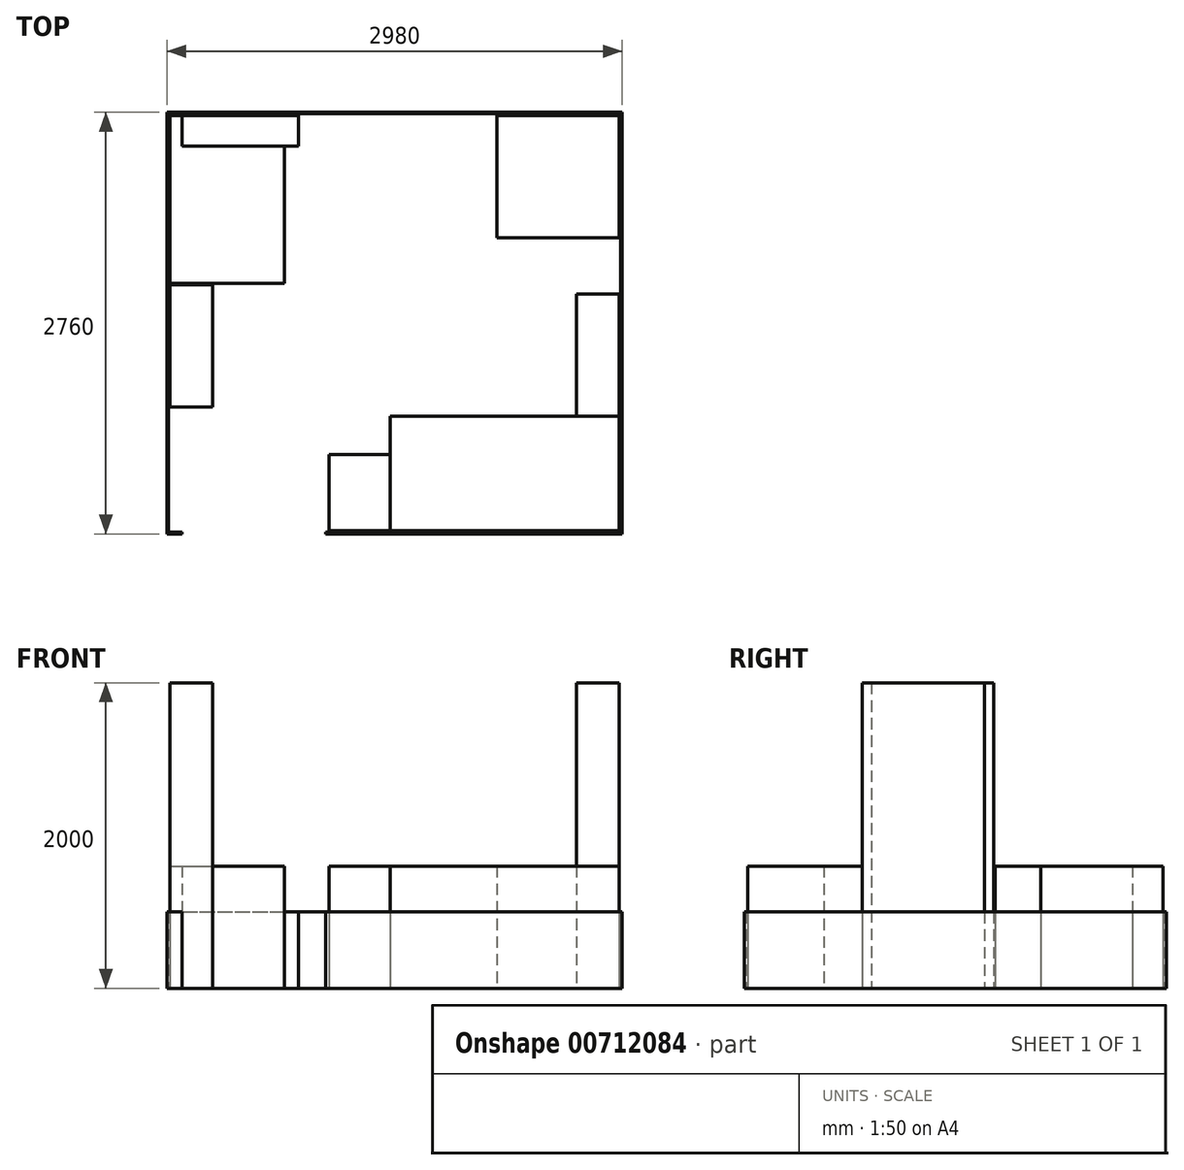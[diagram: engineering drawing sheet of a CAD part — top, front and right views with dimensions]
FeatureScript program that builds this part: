
annotation { "Feature Type Name" : "Feature", "Feature Type Description" : "" }
export const myFeature = defineFeature(function(context is Context, id is Id, definition is map)
    precondition{}
    {
        {
            var Q0;
            Q0=qCreatedBy(makeId("Top.planeOp"),FACE);
            var sketch = newSketch(context, id + "F0", { "sketchPlane" : qUnion([Q0])});
            skLineSegment(sketch, "E0.bottom", {"start": v(-1490, 1990) * mm, "end": v(1470, 1990) * mm});
            skLineSegment(sketch, "E0.top", {"start": v(-1490, -750) * mm, "end": v(-1400, -750) * mm});
            skLineSegment(sketch, "E0.left", {"start": v(-1490, 1990) * mm, "end": v(-1490, -750) * mm});
            skLineSegment(sketch, "E0.right", {"start": v(1470, 1990) * mm, "end": v(1470, -750) * mm});
            skLineSegment(sketch, "E1.0", {"start": v(-1500, 2000) * mm, "end": v(-1500, -760) * mm});
            skLineSegment(sketch, "E1.1", {"start": v(-1500, 2000) * mm, "end": v(1480, 2000) * mm});
            skLineSegment(sketch, "E1.2", {"start": v(1480, 2000) * mm, "end": v(1480, -760) * mm});
            skLineSegment(sketch, "E1.3", {"start": v(-1500, -760) * mm, "end": v(-1400, -760) * mm});
            skLineSegment(sketch, "E2", {"start": v(-1400, -750) * mm, "end": v(-1400, -760) * mm});
            skLineSegment(sketch, "E3", {"start": v(-460, -750) * mm, "end": v(-460, -760) * mm});
            skLineSegment(sketch, "E4.trimOffspring", {"start": v(-460, -750) * mm, "end": v(1470, -750) * mm});
            skLineSegment(sketch, "E5.trimOffspring", {"start": v(-460, -760) * mm, "end": v(1480, -760) * mm});
            skLineSegment(sketch, "E6.bottom", {"start": v(1180, 810) * mm, "end": v(1460, 810) * mm});
            skLineSegment(sketch, "E6.top", {"start": v(1180, 10) * mm, "end": v(1460, 10) * mm});
            skLineSegment(sketch, "E6.left", {"start": v(1180, 810) * mm, "end": v(1180, 10) * mm});
            skLineSegment(sketch, "E6.right", {"start": v(1460, 810) * mm, "end": v(1460, 10) * mm});
            skLineSegment(sketch, "E7.bottom", {"start": v(-1480, 70) * mm, "end": v(-1200, 70) * mm});
            skLineSegment(sketch, "E7.top", {"start": v(-1480, 870) * mm, "end": v(-1200, 870) * mm});
            skLineSegment(sketch, "E7.left", {"start": v(-1480, 70) * mm, "end": v(-1480, 870) * mm});
            skLineSegment(sketch, "E7.right", {"start": v(-1200, 70) * mm, "end": v(-1200, 870) * mm});
            skLineSegment(sketch, "E8.bottom", {"start": v(660, 1980) * mm, "end": v(1460, 1980) * mm});
            skLineSegment(sketch, "E8.top", {"start": v(660, 1180) * mm, "end": v(1460, 1180) * mm});
            skLineSegment(sketch, "E8.left", {"start": v(660, 1980) * mm, "end": v(660, 1180) * mm});
            skLineSegment(sketch, "E8.right", {"start": v(1460, 1980) * mm, "end": v(1460, 1180) * mm});
            skLineSegment(sketch, "E9.bottom", {"start": v(-40, -740) * mm, "end": v(1460, -740) * mm});
            skLineSegment(sketch, "E9.top", {"start": v(-40, 10) * mm, "end": v(1460, 10) * mm});
            skLineSegment(sketch, "E9.left", {"start": v(-40, -740) * mm, "end": v(-40, 10) * mm});
            skLineSegment(sketch, "E9.right", {"start": v(1460, -740) * mm, "end": v(1460, 10) * mm});
            skLineSegment(sketch, "E10.bottom", {"start": v(-1400, 1980) * mm, "end": v(-640, 1980) * mm});
            skLineSegment(sketch, "E10.top", {"start": v(-1400, 1780) * mm, "end": v(-640, 1780) * mm});
            skLineSegment(sketch, "E10.left", {"start": v(-1400, 1980) * mm, "end": v(-1400, 1780) * mm});
            skLineSegment(sketch, "E10.right", {"start": v(-640, 1980) * mm, "end": v(-640, 1780) * mm});
            skLineSegment(sketch, "E11.bottom", {"start": v(-1480, 1980) * mm, "end": v(-730, 1980) * mm});
            skLineSegment(sketch, "E11.top", {"start": v(-1480, 880) * mm, "end": v(-730, 880) * mm});
            skLineSegment(sketch, "E11.left", {"start": v(-1480, 1980) * mm, "end": v(-1480, 880) * mm});
            skLineSegment(sketch, "E11.right", {"start": v(-730, 1980) * mm, "end": v(-730, 880) * mm});
            skLineSegment(sketch, "E12.bottom", {"start": v(-440, -740) * mm, "end": v(-40, -740) * mm});
            skLineSegment(sketch, "E12.top", {"start": v(-440, -240) * mm, "end": v(-40, -240) * mm});
            skLineSegment(sketch, "E12.left", {"start": v(-440, -740) * mm, "end": v(-440, -240) * mm});
            skLineSegment(sketch, "E12.right", {"start": v(-40, -740) * mm, "end": v(-40, -240) * mm});
            skSolve(sketch);
        }
        {
            var Q0;
            Q0=makeQuery(id+"F0.imprint","IMPRINT",FACE,{"disambiguationData":[TD([[makeQuery(id+"F0.imprint","IMPRINT",EDGE,{"derivedFrom":sQuery(id+"F0.wireOp",EDGE,"E0.bottom")}),1.0]])]});
            extrude(context, id + "F1", {"entities" : qUnion([Q0]), "depth" : 500 * mm, "offsetDistance" : 25 * mm});
        }
        {
            var Q0;
            Q0=makeQuery(id+"F0.imprint","IMPRINT",FACE,{"disambiguationData":[TD([[makeQuery(id+"F0.imprint","IMPRINT",EDGE,{"derivedFrom":sQuery(id+"F0.wireOp",EDGE,"E7.bottom")}),1.0]])]});
            extrude(context, id + "F2", {"entities" : qUnion([Q0]), "depth" : 2000 * mm, "offsetDistance" : 25 * mm});
        }
        {
            var Q0;
            Q0=makeQuery(id+"F0.imprint","IMPRINT",FACE,{"disambiguationData":[TD([[makeQuery(id+"F0.imprint","IMPRINT",EDGE,{"derivedFrom":sQuery(id+"F0.wireOp",EDGE,"E10.bottom")}),-1.0]])]});
            extrude(context, id + "F3", {"entities" : qUnion([Q0]), "depth" : 500 * mm, "offsetDistance" : 25 * mm});
        }
        {
            var Q0;
            Q0=makeQuery(id+"F0.imprint","IMPRINT",FACE,{"disambiguationData":[TD([[makeQuery(id+"F0.imprint","IMPRINT",EDGE,{"derivedFrom":sQuery(id+"F0.wireOp",EDGE,"E11.bottom")}),-1.0]])]});
            var Q1;
            {var subQ2=sQuery(id+"F0.wireOp",EDGE,"E10.left");Q1=makeQuery(id+"F0.imprint","IMPRINT",FACE,{"disambiguationData":[TD([[makeQuery(id+"F0.imprint","IMPRINT",EDGE,{"derivedFrom":subQ2}),-1.0]])]});}
            extrude(context, id + "F4", {"entities" : qUnion([Q0, Q1]), "depth" : 800 * mm, "offsetDistance" : 25 * mm});
        }
        {
            var Q0;
            Q0=makeQuery(id+"F0.imprint","IMPRINT",FACE,{"disambiguationData":[TD([[makeQuery(id+"F0.imprint","IMPRINT",EDGE,{"derivedFrom":sQuery(id+"F0.wireOp",EDGE,"E9.bottom")}),1.0]])]});
            extrude(context, id + "F5", {"entities" : qUnion([Q0]), "depth" : 800 * mm, "offsetDistance" : 25 * mm});
        }
        {
            var Q0;
            Q0=makeQuery(id+"F0.imprint","IMPRINT",FACE,{"disambiguationData":[TD([[makeQuery(id+"F0.imprint","IMPRINT",EDGE,{"derivedFrom":sQuery(id+"F0.wireOp",EDGE,"E6.bottom")}),-1.0]])]});
            extrude(context, id + "F6", {"entities" : qUnion([Q0]), "depth" : 2000 * mm, "offsetDistance" : 25 * mm});
        }
        {
            var Q0;
            Q0=makeQuery(id+"F0.imprint","IMPRINT",FACE,{"disambiguationData":[TD([[makeQuery(id+"F0.imprint","IMPRINT",EDGE,{"derivedFrom":sQuery(id+"F0.wireOp",EDGE,"E8.bottom")}),-1.0]])]});
            extrude(context, id + "F7", {"entities" : qUnion([Q0]), "depth" : 800 * mm, "offsetDistance" : 25 * mm});
        }
        {
            var Q0;
            Q0=makeQuery(id+"F0.imprint","IMPRINT",FACE,{"disambiguationData":[TD([[makeQuery(id+"F0.imprint","IMPRINT",EDGE,{"derivedFrom":sQuery(id+"F0.wireOp",EDGE,"E12.bottom")}),1.0]])]});
            extrude(context, id + "F8", {"entities" : qUnion([Q0]), "depth" : 800 * mm, "offsetDistance" : 25 * mm});
        }
    });
